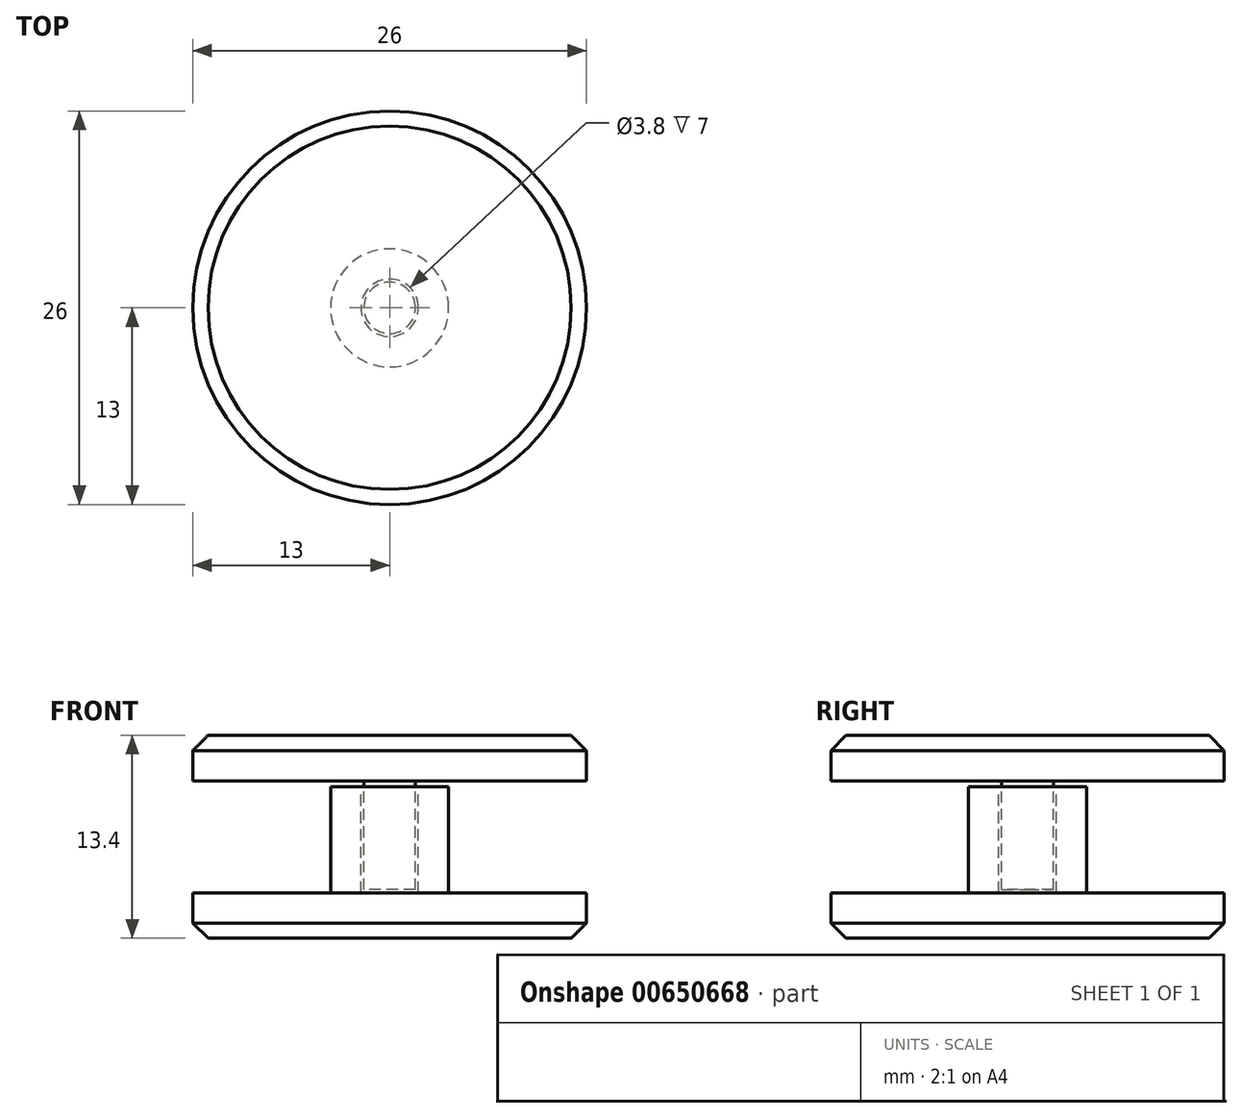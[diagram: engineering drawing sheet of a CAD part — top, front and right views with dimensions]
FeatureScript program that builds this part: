
annotation { "Feature Type Name" : "Feature", "Feature Type Description" : "" }
export const myFeature = defineFeature(function(context is Context, id is Id, definition is map)
    precondition{}
    {
        {
            var Q0;
            Q0=qCreatedBy(makeId("Front.planeOp"),FACE);
            var sketch = newSketch(context, id + "F0", { "sketchPlane" : qUnion([Q0])});
            skLineSegment(sketch, "E0", {"start": v(0, 0) * mm, "end": v(-13, 0) * mm});
            skLineSegment(sketch, "E1", {"start": v(-13, 0) * mm, "end": v(-13, 3) * mm});
            skLineSegment(sketch, "E2", {"start": v(-13, 3) * mm, "end": v(-3.9, 3) * mm});
            skLineSegment(sketch, "E3", {"start": v(-3.9, 3) * mm, "end": v(-3.9, 10) * mm});
            skLineSegment(sketch, "E4", {"start": v(-3.9, 10) * mm, "end": v(-1.9, 10) * mm});
            skLineSegment(sketch, "E5", {"start": v(-1.9, 10) * mm, "end": v(-1.9, 3) * mm});
            skLineSegment(sketch, "E6", {"start": v(-1.9, 3) * mm, "end": v(0, 3) * mm});
            skLineSegment(sketch, "E7", {"start": v(0, 3) * mm, "end": v(0, 0) * mm});
            skLineSegment(sketch, "E8", {"start": v(-13, 0) * mm, "end": v(-13, 13.58) * mm, "construction": true});
            skSolve(sketch);
        }
        {
            var Q0;
            Q0=makeQuery(id+"F0.imprint","IMPRINT",FACE,{"disambiguationData":[TD([[makeQuery(id+"F0.imprint","IMPRINT",EDGE,{"derivedFrom":sQuery(id+"F0.wireOp",EDGE,"E0")}),-1.0]])]});
            var Q1;
            Q1=sQuery(id+"F0.wireOp",EDGE,"E7");
            revolve(context, id + "F1", {"entities" : qUnion([Q0]), "axis" : qUnion([Q1]), "revolveType" : RevolveType.FULL});
        }
        {
            var Q0;
            Q0=makeQuery(id+"F1.opRevolve","SWEPT_EDGE",EDGE,{"disambiguationData":[OSD([sQuery(id+"F0.wireOp",EDGE,"E0"),sQuery(id+"F0.wireOp",EDGE,"E1")])]});
            chamfer(context, id + "F2", {"entities" : qUnion([Q0]), "width" : 1 * mm, "tangentPropagation" : true});
        }
        {
            var Q0;
            Q0=qCreatedBy(makeId("Front.planeOp"),FACE);
            var sketch = newSketch(context, id + "F3", { "sketchPlane" : qUnion([Q0])});
            skLineSegment(sketch, "E9", {"start": v(0, 0) * mm, "end": v(0, 23.62) * mm, "construction": true});
            skLineSegment(sketch, "E10", {"start": v(0, 3.2) * mm, "end": v(-1.7, 3.2) * mm});
            skLineSegment(sketch, "E11", {"start": v(-1.7, 3.2) * mm, "end": v(-1.7, 10.4) * mm});
            skLineSegment(sketch, "E12", {"start": v(-1.7, 10.4) * mm, "end": v(-15.37, 10.4) * mm, "construction": true});
            skLineSegment(sketch, "E13", {"start": v(-1.7, 10.4) * mm, "end": v(-13, 10.4) * mm});
            skLineSegment(sketch, "E14", {"start": v(-13, 10.4) * mm, "end": v(-13, 13.4) * mm});
            skLineSegment(sketch, "E15", {"start": v(-13, 13.4) * mm, "end": v(0, 13.4) * mm});
            skLineSegment(sketch, "E16", {"start": v(0, 13.4) * mm, "end": v(0, 3.2) * mm});
            skSolve(sketch);
        }
        {
            var Q0;
            Q0=makeQuery(id+"F3.imprint","IMPRINT",FACE,{"disambiguationData":[TD([[makeQuery(id+"F3.imprint","IMPRINT",EDGE,{"derivedFrom":sQuery(id+"F3.wireOp",EDGE,"E10")}),-1.0]])]});
            var Q1;
            Q1=sQuery(id+"F3.wireOp",EDGE,"E16");
            revolve(context, id + "F4", {"entities" : qUnion([Q0]), "axis" : qUnion([Q1]), "revolveType" : RevolveType.FULL});
        }
        {
            var Q0;
            Q0=makeQuery(id+"F4.opRevolve","SWEPT_EDGE",EDGE,{"disambiguationData":[OSD([sQuery(id+"F3.wireOp",EDGE,"E14"),sQuery(id+"F3.wireOp",EDGE,"E15")])]});
            chamfer(context, id + "F5", {"entities" : qUnion([Q0]), "width" : 1 * mm, "tangentPropagation" : true});
        }
    });
